# Revit family: 45721CHN_new
name_source: partatom
category: Furniture
revit_build: Autodesk Revit 2018 (Build: 20170223_1515(x64)
units: mm (PartAtom-declared; Revit-internal decimal feet)

## family parameters
Always vertical = No
Cut with Voids When Loaded = No
OmniClass Number = 23.40.20.00
OmniClass Title = General Furniture and Specialties
Room Calculation Point = No
Shared = No
Work Plane-Based = Yes

## types (3) — shared parameters
Always visible = Yes
BIMobject category = Other Sanitary
Default Elevation = 1219.2 mm  [stored 4 ft]
Design country = Germany
EAN code = 4059625209011
Edition number = 1
IFC Classification = Sanitary Terminal
Installation instructions = https://www.axor-design.com
Manufacturer country = Germany
Manufacturer name = AXOR
Material 1 = AXOR - AXOR One - Graphite
Material main = Chrome
Product Guid = 55523f66-d679-4ca3-97f2-6cae77ffee3c
Product SKU = 45721CHN
Product data url = https://www.bimobject.com
Product family = AXOR One
Product group = Shower support
Product name = 45721CHN AXOR One Shower holder
Product url = https://www.axor-design.com
QR code = https://www.bimobject.com
Technical description = https://www.axor-design.com

## per-type parameters (varying)
| type | Material 2 |
| 997 Polished Gold Optic | AXOR - AXOR One - 997 Polished Gold Optic |
| 347 Brushed Black Chrome | AXOR - AXOR One - 347 Brushed Black Chrome |
| 007 Chrome | AXOR - AXOR One - 007 Chrome |

note: [stored X ft] marks values corroborated as IEEE doubles in the binary element streams (Revit-internal decimal feet)

## geometry (parser evidence)
native form markers: Sweep x3
no freeform markers — native parametric forms only
